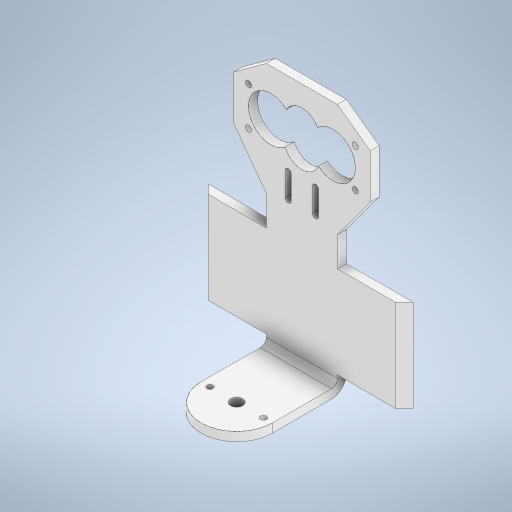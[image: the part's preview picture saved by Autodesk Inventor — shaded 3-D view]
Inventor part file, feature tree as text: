
AUTODESK INVENTOR PART (.ipt)
format: ipt  version: 2023 (Build 270158000, 158)  size: 344,576 bytes
history: native  units: in
note: dims shown in document units (in); Inventor stores cm internally (conversion verified against a paired STEP export)
features: extrude x3, sketch x3, chamfer x1
ambient origin geometry x8: Origin, YZ Plane, XZ Plane, XY Plane, X Axis, Y Axis, Z Axis, Center Point
bodies: Solid1 (feature_tree)
feature tree (7):
  extrude  "Extrusion1"  TaperAngle=0.0deg  [1 undecoded]
  extrude  "Extrusion2"  Depth=0.0787in TaperAngle=45.0deg
  extrude  "Extrusion3"  [1 undecoded]
  chamfer  "Chamfer1"  [1 undecoded]
  sketch  "Sketch1"  dims[d0=0.0394in d1=0.0in d7=0.0in d8=0.0in]
  sketch  "Sketch3"  dims[d9=0.0787in d10=0.0in d11=0.0787in d12=0.0787in d13=45.0deg]
  sketch  "Sketch4"
note: 3 required parameter values undecoded (feature->parameter linkage not recoverable at this tier; creation-order binding heuristic only, values carry confidence <= 0.55)
